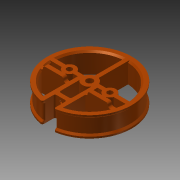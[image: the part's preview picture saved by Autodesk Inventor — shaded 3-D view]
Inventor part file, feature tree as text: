
AUTODESK INVENTOR PART (.ipt)
format: ipt  version: 2013 (Build 170138000, 138)  size: 542,720 bytes
history: native  units: mm
features: sketch x17, extrude x16, projected_geometry x9, fillet x4, chamfer x1, shell x1, rib x1
ambient origin geometry x8: Origin, YZ Plane, XZ Plane, XY Plane, X Axis, Y Axis, Z Axis, Center Point
bodies: Solid1 (feature_tree)
feature tree (49):
  extrude  "Extrusion1"  Depth=25.0mm TaperAngle=0.0deg
  extrude  "Extrusion2"  Depth=4.0mm TaperAngle=0.0deg
  extrude  "Extrusion3"  Depth=4.0mm TaperAngle=45.0deg
  chamfer  "Chamfer1"  Distance=2.0mm
  extrude  "Extrusion4"  Depth=25.0mm TaperAngle=0.0deg
  extrude  "Extrusion6"  Depth=14.395236mm
  extrude  "Extrusion16"  Depth=2.0mm
  fillet  "Fillet4"  Radius=5.0mm
  shell  "Shell1"  Thickness=10.0mm
  rib  "Rib1"
  extrude  "Extrusion17"  Depth=5.0mm
  extrude  "Extrusion18"  Depth=5.6mm
  extrude  "Extrusion19"  Depth=2.0mm
  fillet  "Fillet5"  Radius=25.0mm
  extrude  "Extrusion20"  Depth=15.0mm
  extrude  "Extrusion21"  Depth=6.5mm
  extrude  "Extrusion22"  Depth=3.1mm
  extrude  "Extrusion23"  Depth=12.5mm
  extrude  "Extrusion24"  Depth=5.0mm TaperAngle=0.0deg
  extrude  "Extrusion25"  Depth=5.0mm TaperAngle=0.0deg
  fillet  "Fillet6"  Radius=25.0mm
  fillet  "Fillet7"  Radius=25.0mm
  extrude  "Extrusion28"  Depth=5.0mm TaperAngle=0.0deg
  sketch  "Sketch1"  dims[d0=100.0mm d2=25.0mm d3=0.0mm]
  sketch  "Sketch2"  dims[d4=4.0mm d5=4.0mm d6=0.0mm]
  sketch  "Sketch3"  dims[d7=4.0mm d8=0.0mm d9=4.0mm d10=2.0mm d11=45.0deg]
  sketch  "Sketch4"  dims[d12=2.0mm d13=2.0mm d14=0.0mm]
  sketch  "Sketch6"  dims[d19=8.1mm d21=25.0mm d22=0.0mm]
  sketch  "Sketch21"  dims[d28=15.0mm d107=14.395236mm]
  sketch  "Sketch22"  dims[d108=10.0mm d109=0.0mm d110=2.0mm d111=5.0mm]
  projected_geometry  "Projected Loop7"
  sketch  "Sketch23"  dims[d112=5.0mm d113=1.0mm d114=0.0mm d115=0.0mm d116=1.0mm d117=1.0mm d118=10.0mm d119=0.0mm]
  sketch  "Sketch24"  dims[d120=3.1mm d122=5.0mm]
  sketch  "Sketch25"  dims[d123=10.0mm d124=0.0mm d125=5.6mm]
  sketch  "Sketch26"  dims[d126=2.5mm d127=0.0mm d128=2.0mm d129=25.0mm]
  sketch  "Sketch27"  dims[d130=25.0mm d131=15.0mm]
  sketch  "Sketch28"  dims[d132=2.5mm d133=0.0mm d134=6.5mm]
  projected_geometry  "Projected Loop8"
  sketch  "Sketch29"  dims[d136=2.5mm d137=0.0mm d138=3.1mm]
  sketch  "Sketch30"  dims[d140=2.5mm d141=0.0mm d142=12.5mm]
  sketch  "Sketch31"  dims[d143=5.0mm d144=5.0mm d145=0.0mm]
  sketch  "Sketch34"  dims[d146=5.0mm d148=5.0mm d149=0.0mm d151=25.0mm d152=25.0mm d153=5.0mm d154=0.0mm d155=2.5mm d156=0.5mm d168=10.0mm d169=0.0mm]
  projected_geometry  "Projected Loop13"
  projected_geometry  "Projected Loop14"
  projected_geometry  "Projected Loop15"
  projected_geometry  "Projected Loop16"
  projected_geometry  "Projected Loop17"
  projected_geometry  "Projected Loop18"
  projected_geometry  "Projected Loop19"
